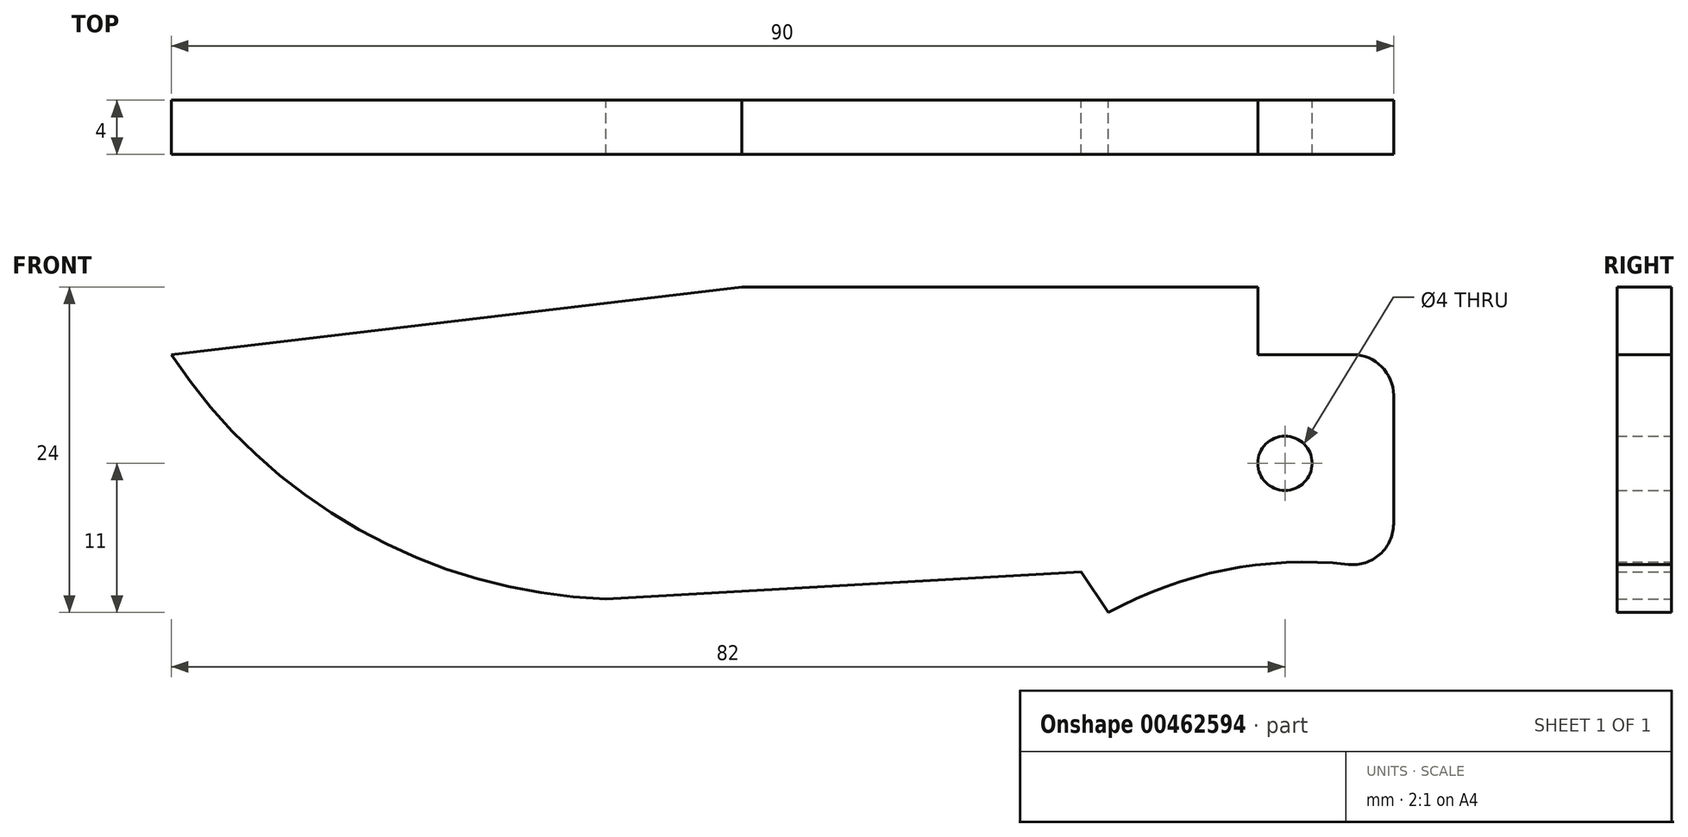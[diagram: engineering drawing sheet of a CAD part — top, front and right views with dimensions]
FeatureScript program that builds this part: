
annotation { "Feature Type Name" : "Feature", "Feature Type Description" : "" }
export const myFeature = defineFeature(function(context is Context, id is Id, definition is map)
    precondition{}
    {
        {
            var Q0;
            Q0=qCreatedBy(makeId("Front.planeOp"),FACE);
            var sketch = newSketch(context, id + "F0", { "sketchPlane" : qUnion([Q0])});
            skCircle(sketch, "E0", {"center": v(0, 0) * mm, "radius": 2 * mm});
            skLineSegment(sketch, "E1", {"start": v(-2, 8) * mm, "end": v(8, 8) * mm});
            skLineSegment(sketch, "E2", {"start": v(8, 8) * mm, "end": v(8, -8) * mm});
            skLineSegment(sketch, "E3", {"start": v(-2, 8) * mm, "end": v(-2, 13) * mm});
            skLineSegment(sketch, "E4", {"start": v(-2, 13) * mm, "end": v(-40, 13) * mm});
            skArc(sketch, "E5", {"start": v(-82, 8) * mm, "mid": v(-68.19, -4.89) * mm, "end": v(-50, -10) * mm});
            skLineSegment(sketch, "E6", {"start": v(-50, -10) * mm, "end": v(-15, -8) * mm});
            skLineSegment(sketch, "E7", {"start": v(-15, -8) * mm, "end": v(-13, -11) * mm});
            skArc(sketch, "E8", {"start": v(8, -8) * mm, "mid": v(-2.77, -7.58) * mm, "end": v(-13, -11) * mm});
            skLineSegment(sketch, "E9", {"start": v(-82, 8) * mm, "end": v(-40, 13) * mm});
            skSolve(sketch);
        }
        {
            var Q0;
            Q0=makeQuery(id+"F0.imprint","IMPRINT",FACE,{"disambiguationData":[TD([[makeQuery(id+"F0.imprint","IMPRINT",EDGE,{"derivedFrom":sQuery(id+"F0.wireOp",EDGE,"E0")}),-1.0]])]});
            extrude(context, id + "F1", {"entities" : qUnion([Q0]), "depth" : 4 * mm});
        }
        {
            var Q0;
            Q0=makeQuery(id+"F1.opExtrude","SWEPT_EDGE",EDGE,{"disambiguationData":[OSD([sQuery(id+"F0.wireOp",EDGE,"E1"),sQuery(id+"F0.wireOp",EDGE,"E2")])]});
            var Q1;
            Q1=makeQuery(id+"F1.opExtrude","SWEPT_EDGE",EDGE,{"disambiguationData":[OSD([sQuery(id+"F0.wireOp",EDGE,"E2"),sQuery(id+"F0.wireOp",EDGE,"E8")])]});
            fillet(context, id + "F2", {"entities" : qUnion([Q0, Q1]), "radius" : 3 * mm, "tangentPropagation" : true, "allowEdgeOverflow" : false});
        }
    });
